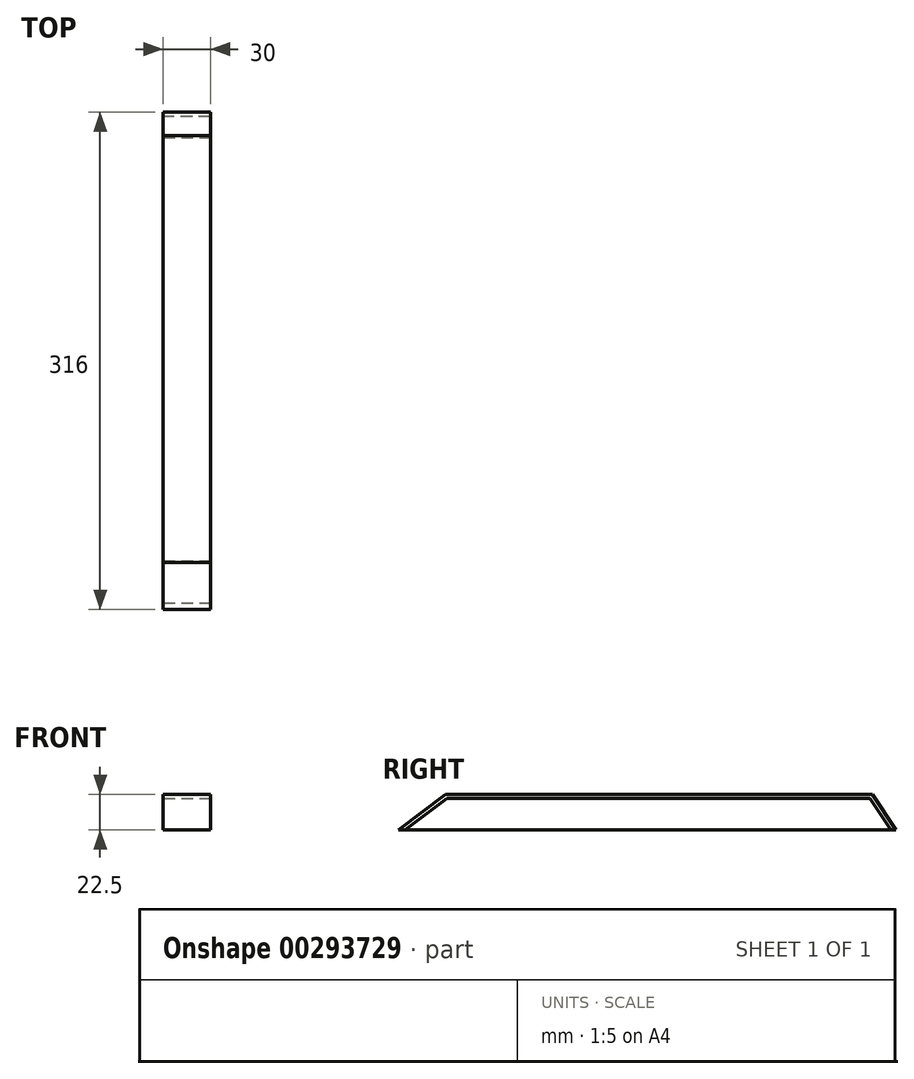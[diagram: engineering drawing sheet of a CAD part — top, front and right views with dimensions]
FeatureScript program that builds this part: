
annotation { "Feature Type Name" : "Feature", "Feature Type Description" : "" }
export const myFeature = defineFeature(function(context is Context, id is Id, definition is map)
    precondition{}
    {
        {
            var Q0;
            Q0=qCreatedBy(makeId("Top.planeOp"),FACE);
            var sketch = newSketch(context, id + "F0", { "sketchPlane" : qUnion([Q0])});
            skLineSegment(sketch, "E0.bottom", {"start": v(-15, 158) * mm, "end": v(15, 158) * mm});
            skLineSegment(sketch, "E0.top", {"start": v(-15, -158) * mm, "end": v(15, -158) * mm});
            skLineSegment(sketch, "E0.left", {"start": v(-15, 158) * mm, "end": v(-15, -158) * mm});
            skLineSegment(sketch, "E0.right", {"start": v(15, 158) * mm, "end": v(15, -158) * mm});
            skPoint(sketch, "E0.middle", {"position": v(0, 0) * mm});
            skSolve(sketch);
        }
        {
            var Q0;
            Q0=qSketchRegion(id+"F0",true);
            extrude(context, id + "F1", {"entities" : qUnion([Q0]), "depth" : 5 * mm});
        }
        {
            var Q0;
            Q0=makeQuery(id+"F1.opExtrude","CAP_FACE",FACE,{"disambiguationData":[OSD([sQuery(id+"F0.wireOp",EDGE,"E0.bottom"),sQuery(id+"F0.wireOp",EDGE,"E0.top"),sQuery(id+"F0.wireOp",EDGE,"E0.left"),sQuery(id+"F0.wireOp",EDGE,"E0.right")])],"isStart":true});
            extrude(context, id + "F2", {"entities" : qUnion([Q0]), "operationType" : NewBodyOperationType.ADD, "depth" : 17.5 * mm});
        }
        {
            var Q0;
            Q0=makeQuery(id+"F1.opExtrude","CAP_EDGE",EDGE,{"disambiguationData":[OSD([sQuery(id+"F0.wireOp",EDGE,"E0.bottom")])],"isStart":false});
            chamfer(context, id + "F3", {"entities" : qUnion([Q0]), "chamferType" : ChamferType.TWO_OFFSETS, "width1" : 22.5 * mm, "oppositeDirection" : false, "width2" : 15 * mm, "tangentPropagation" : true});
        }
        {
            var Q0;
            Q0=makeQuery(id+"F1.opExtrude","CAP_EDGE",EDGE,{"disambiguationData":[OSD([sQuery(id+"F0.wireOp",EDGE,"E0.top")])],"isStart":false});
            chamfer(context, id + "F4", {"entities" : qUnion([Q0]), "chamferType" : ChamferType.TWO_OFFSETS, "width1" : 30 * mm, "oppositeDirection" : false, "width2" : 22.5 * mm, "tangentPropagation" : true});
        }
        {
            var Q0;
            Q0=makeQuery(id+"F2.opExtrude","CAP_FACE",FACE,{"disambiguationData":[OSD([sQuery(id+"F0.wireOp",EDGE,"E0.bottom"),sQuery(id+"F0.wireOp",EDGE,"E0.top"),sQuery(id+"F0.wireOp",EDGE,"E0.left"),sQuery(id+"F0.wireOp",EDGE,"E0.right")])],"isStart":false});
            shell(context, id + "F5", {"entities" : qUnion([Q0]), "thickness" : 2.5 * mm});
        }
        {
            var Q0;
            Q0=makeQuery(id+"F5.opShell","OFFSET_FACE",FACE,{"disambiguationData":[OSD([sQuery(id+"F0.wireOp",EDGE,"E0.left")])]});
            extrude(context, id + "F6", {"entities" : qUnion([Q0]), "operationType" : NewBodyOperationType.REMOVE, "oppositeDirection" : true, "depth" : 2.4 * mm});
        }
        {
            var Q0;
            Q0=makeQuery(id+"F5.opShell","OFFSET_FACE",FACE,{"disambiguationData":[OSD([sQuery(id+"F0.wireOp",EDGE,"E0.right")])]});
            extrude(context, id + "F7", {"entities" : qUnion([Q0]), "operationType" : NewBodyOperationType.REMOVE, "oppositeDirection" : true, "depth" : 25 * mm});
        }
    });
